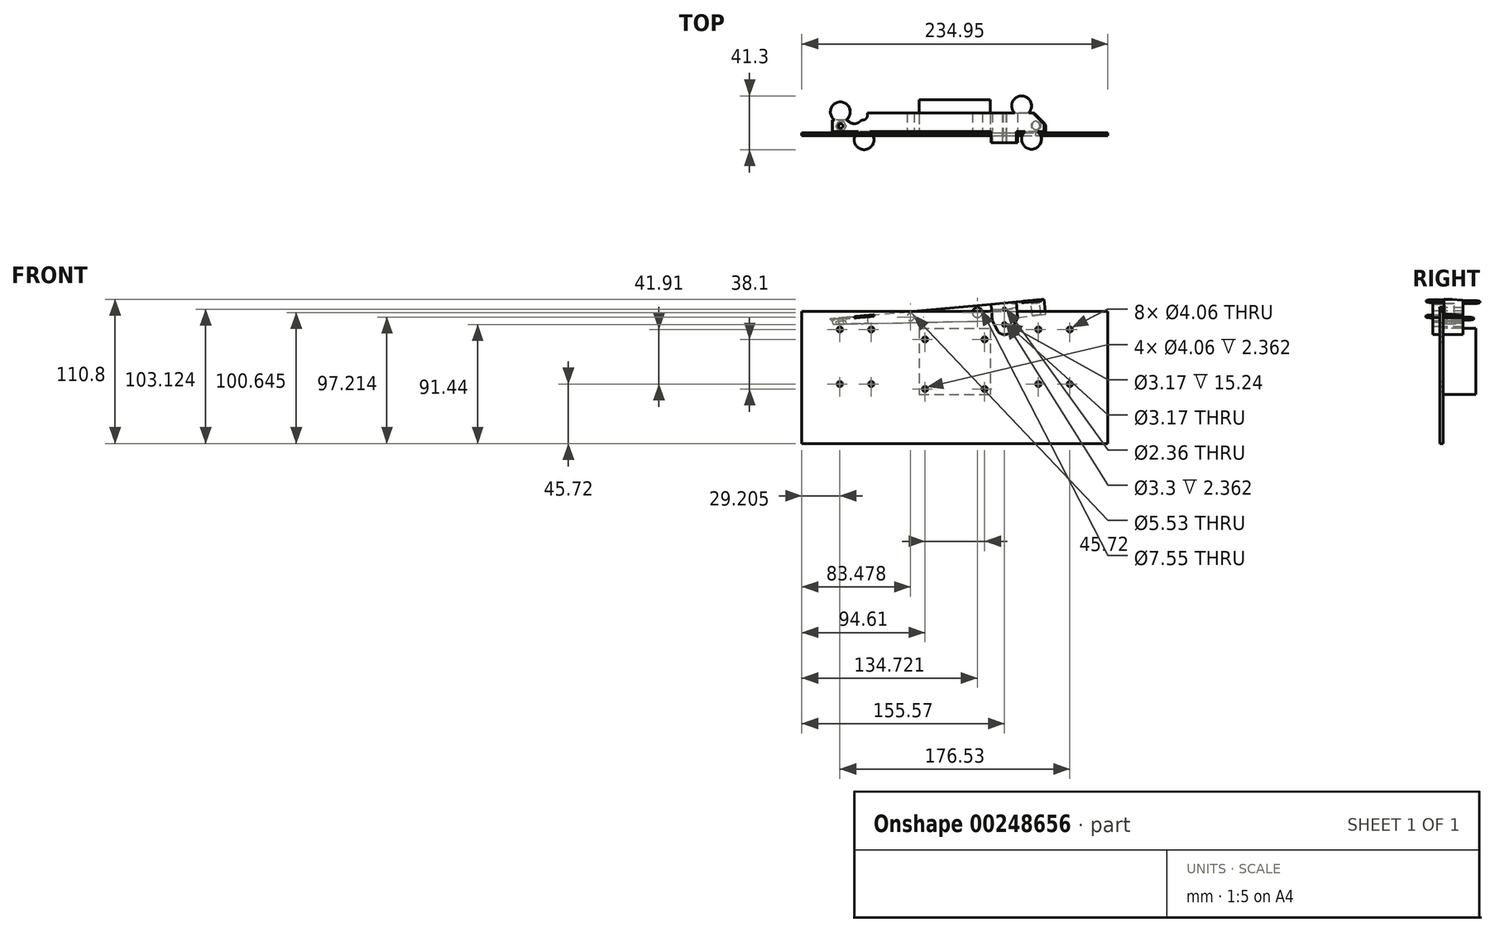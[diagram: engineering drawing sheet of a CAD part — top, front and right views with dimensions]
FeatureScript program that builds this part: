
annotation { "Feature Type Name" : "Feature", "Feature Type Description" : "" }
export const myFeature = defineFeature(function(context is Context, id is Id, definition is map)
    precondition{}
    {
        {
            var Q0;
            Q0=qCreatedBy(makeId("Front.planeOp"),FACE);
            var sketch = newSketch(context, id + "F0", { "sketchPlane" : qUnion([Q0])});
            skCircle(sketch, "E0", {"center": v(0, 0) * mm, "radius": 16.51 * mm, "construction": true});
            skLineSegment(sketch, "E1", {"start": v(-132.08, 4.54) * mm, "end": v(30.48, 19.36) * mm});
            skLineSegment(sketch, "E2", {"start": v(-132.08, 4.54) * mm, "end": v(-131.69, 0.24) * mm});
            skLineSegment(sketch, "E3", {"start": v(-131.69, 0.24) * mm, "end": v(-9.18, 2.82) * mm});
            skLineSegment(sketch, "E4", {"start": v(-9.18, 2.82) * mm, "end": v(-3.8, -7.62) * mm});
            skLineSegment(sketch, "E5", {"start": v(-3.8, -7.62) * mm, "end": v(3.81, -7.62) * mm});
            skLineSegment(sketch, "E6", {"start": v(3.8, -7.62) * mm, "end": v(10.05, 5.45) * mm});
            skLineSegment(sketch, "E7", {"start": v(10.05, 5.45) * mm, "end": v(31.52, 7.97) * mm});
            skLineSegment(sketch, "E8", {"start": v(31.52, 7.97) * mm, "end": v(30.48, 19.36) * mm});
            skCircle(sketch, "E9", {"center": v(0, 0) * mm, "radius": 1.59 * mm});
            skCircle(sketch, "E10", {"center": v(0, 0) * mm, "radius": 11.43 * mm, "construction": true});
            skLineSegment(sketch, "E11", {"start": v(-131.97, 3.37) * mm, "end": v(-0.3, 11.43) * mm});
            skLineSegment(sketch, "E12", {"start": v(-0.3, 11.43) * mm, "end": v(30.64, 17.62) * mm});
            skLineSegment(sketch, "E13", {"start": v(-9.18, 2.82) * mm, "end": v(-9.92, 10.84) * mm});
            skLineSegment(sketch, "E14", {"start": v(10.05, 5.45) * mm, "end": v(9.33, 13.35) * mm});
            skLineSegment(sketch, "E15", {"start": v(-9.92, 10.84) * mm, "end": v(-10.35, 15.63) * mm});
            skLineSegment(sketch, "E16", {"start": v(9.33, 13.35) * mm, "end": v(8.96, 17.4) * mm});
            skSolve(sketch);
        }
        {
            var Q0;
            {var subQ0=sQuery(id+"F0.wireOp",EDGE,"E3");Q0=makeQuery(id+"F0.imprint","IMPRINT",FACE,{"disambiguationData":[TD([[makeQuery(id+"F0.imprint","IMPRINT",EDGE,{"derivedFrom":subQ0}),1.0]])]});}
            var Q1;
            {var subQ3=sQuery(id+"F0.wireOp",EDGE,"E15");Q1=makeQuery(id+"F0.imprint","IMPRINT",FACE,{"disambiguationData":[TD([[makeQuery(id+"F0.imprint","IMPRINT",EDGE,{"derivedFrom":subQ3}),1.0]])]});}
            var Q2;
            {var subQ0=sQuery(id+"F0.wireOp",EDGE,"E15");Q2=makeQuery(id+"F0.imprint","IMPRINT",FACE,{"disambiguationData":[TD([[makeQuery(id+"F0.imprint","IMPRINT",EDGE,{"derivedFrom":subQ0}),-1.0]])]});}
            var Q3;
            Q3=makeQuery(id+"F0.imprint","IMPRINT",FACE,{"disambiguationData":[TD([[makeQuery(id+"F0.imprint","IMPRINT",EDGE,{"derivedFrom":sQuery(id+"F0.wireOp",EDGE,"E4")}),1.0]])]});
            var Q4;
            {var subQ0=sQuery(id+"F0.wireOp",EDGE,"E7");Q4=makeQuery(id+"F0.imprint","IMPRINT",FACE,{"disambiguationData":[TD([[makeQuery(id+"F0.imprint","IMPRINT",EDGE,{"derivedFrom":subQ0}),1.0]])]});}
            var Q5;
            {var subQ3=sQuery(id+"F0.wireOp",EDGE,"E16");Q5=makeQuery(id+"F0.imprint","IMPRINT",FACE,{"disambiguationData":[TD([[makeQuery(id+"F0.imprint","IMPRINT",EDGE,{"derivedFrom":subQ3}),-1.0]])]});}
            extrude(context, id + "F1", {"entities" : qUnion([Q0, Q1, Q2, Q3, Q4, Q5]), "oppositeDirection" : true, "depth" : 15.24 * mm, "hasSecondDirection" : true, "secondDirectionOppositeDirection" : false, "secondDirectionDepth" : 7.62 * mm});
        }
        {
            var Q0;
            {var subQ1=sQuery(id+"F0.wireOp",EDGE,"E3");Q0=makeQuery(id+"F0.imprint","IMPRINT",FACE,{"disambiguationData":[TD([[makeQuery(id+"F0.imprint","IMPRINT",EDGE,{"derivedFrom":subQ1}),1.0]])]});}
            var Q1;
            Q1=makeQuery(id+"F0.imprint","IMPRINT",FACE,{"disambiguationData":[TD([[makeQuery(id+"F0.imprint","IMPRINT",EDGE,{"derivedFrom":sQuery(id+"F0.wireOp",EDGE,"E4")}),1.0]])]});
            var Q2;
            {var subQ0=sQuery(id+"F0.wireOp",EDGE,"E7");Q2=makeQuery(id+"F0.imprint","IMPRINT",FACE,{"disambiguationData":[TD([[makeQuery(id+"F0.imprint","IMPRINT",EDGE,{"derivedFrom":subQ0}),1.0]])]});}
            extrude(context, id + "F2", {"entities" : qUnion([Q0, Q1, Q2]), "operationType" : NewBodyOperationType.REMOVE, "depth" : 2.5 * mm});
        }
        {
            var Q0;
            {var subQ0=sQuery(id+"F0.wireOp",EDGE,"E3");Q0=makeQuery(id+"F0.imprint","IMPRINT",FACE,{"disambiguationData":[TD([[makeQuery(id+"F0.imprint","IMPRINT",EDGE,{"derivedFrom":subQ0}),1.0]])]});}
            var Q1;
            {var subQ3=sQuery(id+"F0.wireOp",EDGE,"E15");Q1=makeQuery(id+"F0.imprint","IMPRINT",FACE,{"disambiguationData":[TD([[makeQuery(id+"F0.imprint","IMPRINT",EDGE,{"derivedFrom":subQ3}),1.0]])]});}
            var Q2;
            {var subQ0=sQuery(id+"F0.wireOp",EDGE,"E7");Q2=makeQuery(id+"F0.imprint","IMPRINT",FACE,{"disambiguationData":[TD([[makeQuery(id+"F0.imprint","IMPRINT",EDGE,{"derivedFrom":subQ0}),1.0]])]});}
            var Q3;
            {var subQ3=sQuery(id+"F0.wireOp",EDGE,"E16");Q3=makeQuery(id+"F0.imprint","IMPRINT",FACE,{"disambiguationData":[TD([[makeQuery(id+"F0.imprint","IMPRINT",EDGE,{"derivedFrom":subQ3}),-1.0]])]});}
            extrude(context, id + "F3", {"entities" : qUnion([Q0, Q1, Q2, Q3]), "operationType" : NewBodyOperationType.REMOVE, "depth" : 25.4 * mm, "hasSecondDirection" : true, "secondDirectionOppositeDirection" : true, "secondDirectionDepth" : 0.76 * mm});
        }
        {
            var Q0;
            {var subQ0=sQuery(id+"F0.wireOp",EDGE,"E9");var subQ1=sQuery(id+"F0.wireOp",EDGE,"E8");var subQ2=sQuery(id+"F0.wireOp",EDGE,"E7");var subQ3=sQuery(id+"F0.wireOp",EDGE,"E6");var subQ4=sQuery(id+"F0.wireOp",EDGE,"E5");var subQ5=sQuery(id+"F0.wireOp",EDGE,"E4");var subQ6=sQuery(id+"F0.wireOp",EDGE,"E3");var subQ7=sQuery(id+"F0.wireOp",EDGE,"E2");Q0=makeQuery(id+"F2.boolean.opBoolean","SPLIT",EDGE,{"disambiguationData":[TD([makeQuery(id+"F1.opExtrude","CAP_FACE",FACE,{"disambiguationData":[OSD([sQuery(id+"F0.wireOp",EDGE,"E1"),subQ7,subQ6,subQ5,subQ4,subQ3,subQ2,subQ1,subQ0])],"isStart":false})])],"derivedFrom":makeQuery(id+"F1.opExtrude","SWEPT_EDGE",EDGE,{"disambiguationData":[OSD([subQ5,subQ4])]})});}
            var Q1;
            {var subQ0=sQuery(id+"F0.wireOp",EDGE,"E9");var subQ1=sQuery(id+"F0.wireOp",EDGE,"E8");var subQ2=sQuery(id+"F0.wireOp",EDGE,"E7");var subQ3=sQuery(id+"F0.wireOp",EDGE,"E6");var subQ4=sQuery(id+"F0.wireOp",EDGE,"E5");var subQ5=sQuery(id+"F0.wireOp",EDGE,"E4");var subQ6=sQuery(id+"F0.wireOp",EDGE,"E3");var subQ7=sQuery(id+"F0.wireOp",EDGE,"E2");Q1=makeQuery(id+"F2.boolean.opBoolean","SPLIT",EDGE,{"disambiguationData":[TD([makeQuery(id+"F1.opExtrude","CAP_FACE",FACE,{"disambiguationData":[OSD([sQuery(id+"F0.wireOp",EDGE,"E1"),subQ7,subQ6,subQ5,subQ4,subQ3,subQ2,subQ1,subQ0])],"isStart":true})])],"derivedFrom":makeQuery(id+"F1.opExtrude","SWEPT_EDGE",EDGE,{"disambiguationData":[OSD([subQ5,subQ4])]})});}
            var Q2;
            {var subQ0=sQuery(id+"F0.wireOp",EDGE,"E9");var subQ1=sQuery(id+"F0.wireOp",EDGE,"E8");var subQ2=sQuery(id+"F0.wireOp",EDGE,"E7");var subQ3=sQuery(id+"F0.wireOp",EDGE,"E6");var subQ4=sQuery(id+"F0.wireOp",EDGE,"E5");var subQ5=sQuery(id+"F0.wireOp",EDGE,"E4");var subQ6=sQuery(id+"F0.wireOp",EDGE,"E3");var subQ7=sQuery(id+"F0.wireOp",EDGE,"E2");Q2=makeQuery(id+"F2.boolean.opBoolean","SPLIT",EDGE,{"disambiguationData":[TD([makeQuery(id+"F1.opExtrude","CAP_FACE",FACE,{"disambiguationData":[OSD([sQuery(id+"F0.wireOp",EDGE,"E1"),subQ7,subQ6,subQ5,subQ4,subQ3,subQ2,subQ1,subQ0])],"isStart":true})])],"derivedFrom":makeQuery(id+"F1.opExtrude","SWEPT_EDGE",EDGE,{"disambiguationData":[OSD([subQ4,subQ3])]})});}
            var Q3;
            {var subQ0=sQuery(id+"F0.wireOp",EDGE,"E9");var subQ1=sQuery(id+"F0.wireOp",EDGE,"E8");var subQ2=sQuery(id+"F0.wireOp",EDGE,"E7");var subQ3=sQuery(id+"F0.wireOp",EDGE,"E6");var subQ4=sQuery(id+"F0.wireOp",EDGE,"E5");var subQ5=sQuery(id+"F0.wireOp",EDGE,"E4");var subQ6=sQuery(id+"F0.wireOp",EDGE,"E3");var subQ7=sQuery(id+"F0.wireOp",EDGE,"E2");Q3=makeQuery(id+"F2.boolean.opBoolean","SPLIT",EDGE,{"disambiguationData":[TD([makeQuery(id+"F1.opExtrude","CAP_FACE",FACE,{"disambiguationData":[OSD([sQuery(id+"F0.wireOp",EDGE,"E1"),subQ7,subQ6,subQ5,subQ4,subQ3,subQ2,subQ1,subQ0])],"isStart":false})])],"derivedFrom":makeQuery(id+"F1.opExtrude","SWEPT_EDGE",EDGE,{"disambiguationData":[OSD([subQ4,subQ3])]})});}
            fillet(context, id + "F4", {"entities" : qUnion([Q0, Q1, Q2, Q3]), "radius" : 5.08 * mm, "tangentPropagation" : true, "allowEdgeOverflow" : false});
        }
        {
            var Q0;
            Q0=makeQuery(id+"F1.opExtrude","SWEPT_FACE",FACE,{"disambiguationData":[OSD([sQuery(id+"F0.wireOp",EDGE,"E1")])]});
            var sketch = newSketch(context, id + "F5", { "sketchPlane" : qUnion([Q0])});
            skCircle(sketch, "E17", {"center": v(-124.77, 5.08) * mm, "radius": 1.77 * mm});
            skSolve(sketch);
        }
        {
            var Q0;
            Q0 = qSketchRegion(id + "F5", true);
            extrude(context, id + "F6", {"entities" : qUnion([Q0]), "operationType" : NewBodyOperationType.REMOVE, "endBound" : BoundingType.THROUGH_ALL, "oppositeDirection" : true, "depth" : 25.4 * mm});
        }
        {
            var Q0;
            Q0=qCreatedBy(makeId("Front.planeOp"),FACE);
            var sketch = newSketch(context, id + "F7", { "sketchPlane" : qUnion([Q0])});
            skLineSegment(sketch, "E18.bottom", {"start": v(-155.58, 10.16) * mm, "end": v(79.38, 10.16) * mm});
            skLineSegment(sketch, "E18.top", {"start": v(-155.58, -91.44) * mm, "end": v(79.38, -91.44) * mm});
            skLineSegment(sketch, "E18.left", {"start": v(-155.58, 10.16) * mm, "end": v(-155.58, -91.44) * mm});
            skLineSegment(sketch, "E18.right", {"start": v(79.38, 10.16) * mm, "end": v(79.38, -91.44) * mm});
            skPoint(sketch, "E19", {"position": v(-38.1, 10.16) * mm});
            skLineSegment(sketch, "E20.bottom", {"start": v(-60.96, -11.43) * mm, "end": v(-15.24, -11.43) * mm, "construction": true});
            skLineSegment(sketch, "E20.top", {"start": v(-60.96, -49.53) * mm, "end": v(-15.24, -49.53) * mm, "construction": true});
            skLineSegment(sketch, "E20.left", {"start": v(-60.96, -11.43) * mm, "end": v(-60.96, -49.53) * mm, "construction": true});
            skLineSegment(sketch, "E20.right", {"start": v(-15.24, -11.43) * mm, "end": v(-15.24, -49.53) * mm, "construction": true});
            skPoint(sketch, "E20.middle", {"position": v(-38.1, -30.48) * mm});
            skCircle(sketch, "E21", {"center": v(-60.96, -11.43) * mm, "radius": 2.03 * mm});
            skCircle(sketch, "E22", {"center": v(-15.24, -11.43) * mm, "radius": 2.03 * mm});
            skCircle(sketch, "E23", {"center": v(-60.96, -49.53) * mm, "radius": 2.03 * mm});
            skCircle(sketch, "E24", {"center": v(-15.24, -49.53) * mm, "radius": 2.03 * mm});
            skLineSegment(sketch, "E25", {"start": v(-114.3, -3.81) * mm, "end": v(-114.3, -45.72) * mm, "construction": true});
            skLineSegment(sketch, "E26", {"start": v(38.1, -3.81) * mm, "end": v(38.1, -45.72) * mm, "construction": true});
            skLineSegment(sketch, "E27", {"start": v(-114.3, -3.81) * mm, "end": v(38.1, -3.81) * mm, "construction": true});
            skLineSegment(sketch, "E28", {"start": v(-114.3, -45.72) * mm, "end": v(38.1, -45.72) * mm, "construction": true});
            skCircle(sketch, "E29", {"center": v(0, 0) * mm, "radius": 1.65 * mm});
            skLineSegment(sketch, "E30.bottom", {"start": v(-102.23, -3.81) * mm, "end": v(-126.37, -3.81) * mm, "construction": true});
            skLineSegment(sketch, "E30.top", {"start": v(-102.23, -45.72) * mm, "end": v(-126.37, -45.72) * mm, "construction": true});
            skLineSegment(sketch, "E30.left", {"start": v(-102.23, -3.81) * mm, "end": v(-102.23, -45.72) * mm, "construction": true});
            skLineSegment(sketch, "E30.right", {"start": v(-126.37, -3.81) * mm, "end": v(-126.37, -45.72) * mm, "construction": true});
            skPoint(sketch, "E30.middle", {"position": v(-114.3, -24.77) * mm});
            skLineSegment(sketch, "E31.bottom", {"start": v(50.17, -3.81) * mm, "end": v(26.04, -3.81) * mm, "construction": true});
            skLineSegment(sketch, "E31.top", {"start": v(50.17, -45.72) * mm, "end": v(26.04, -45.72) * mm, "construction": true});
            skLineSegment(sketch, "E31.left", {"start": v(50.17, -3.81) * mm, "end": v(50.17, -45.72) * mm, "construction": true});
            skLineSegment(sketch, "E31.right", {"start": v(26.04, -3.81) * mm, "end": v(26.04, -45.72) * mm, "construction": true});
            skPoint(sketch, "E31.middle", {"position": v(38.1, -24.77) * mm});
            skCircle(sketch, "E32", {"center": v(-102.23, -3.81) * mm, "radius": 2.03 * mm});
            skCircle(sketch, "E33", {"center": v(-126.37, -3.81) * mm, "radius": 2.03 * mm});
            skCircle(sketch, "E34", {"center": v(-126.37, -45.72) * mm, "radius": 2.03 * mm});
            skCircle(sketch, "E35", {"center": v(-102.23, -45.72) * mm, "radius": 2.03 * mm});
            skCircle(sketch, "E36", {"center": v(26.04, -45.72) * mm, "radius": 2.03 * mm});
            skCircle(sketch, "E37", {"center": v(50.17, -45.72) * mm, "radius": 2.03 * mm});
            skCircle(sketch, "E38", {"center": v(50.17, -3.81) * mm, "radius": 2.03 * mm});
            skCircle(sketch, "E39", {"center": v(26.04, -3.81) * mm, "radius": 2.03 * mm});
            skSolve(sketch);
        }
        {
            var Q0;
            Q0 = qSketchRegion(id + "F7", true);
            extrude(context, id + "F8", {"entities" : qUnion([Q0]), "depth" : 2.36 * mm});
        }
        {
            var Q0;
            Q0=makeQuery(id+"F1.opExtrude","SWEPT_FACE",FACE,{"disambiguationData":[OSD([sQuery(id+"F0.wireOp",EDGE,"E1")])]});
            var sketch = newSketch(context, id + "F9", { "sketchPlane" : qUnion([Q0])});
            skLineSegment(sketch, "E40.bottom", {"start": v(-131.12, 15.24) * mm, "end": v(-104.22, 15.24) * mm});
            skLineSegment(sketch, "E40.top", {"start": v(-131.12, 9.65) * mm, "end": v(-107.77, 9.65) * mm});
            skLineSegment(sketch, "E40.left", {"start": v(-131.12, 15.24) * mm, "end": v(-131.12, 9.65) * mm});
            skLineSegment(sketch, "E40.right", {"start": v(-104.22, 15.24) * mm, "end": v(-104.22, 13.2) * mm});
            skPoint(sketch, "E41.visualSharp", {"position": v(-104.22, 9.65) * mm});
            skArc(sketch, "E41.filletArc", {"start": v(-107.77, 9.65) * mm, "mid": v(-105.26, 10.7) * mm, "end": v(-104.22, 13.2) * mm});
            skCircle(sketch, "E42", {"center": v(-114.36, 13.46) * mm, "radius": 6.6 * mm});
            skSolve(sketch);
        }
        {
            var Q0;
            Q0 = qSketchRegion(id + "F9", true);
            extrude(context, id + "F10", {"entities" : qUnion([Q0]), "operationType" : NewBodyOperationType.REMOVE, "endBound" : BoundingType.THROUGH_ALL, "oppositeDirection" : true, "depth" : 25.4 * mm});
        }
        {
            var Q0;
            Q0=makeQuery(id+"F7.imprint","IMPRINT",FACE,{"disambiguationData":[TD([[makeQuery(id+"F7.imprint","IMPRINT",EDGE,{"derivedFrom":sQuery(id+"F7.wireOp",EDGE,"E18.bottom")}),-1.0]])]});
            var sketch = newSketch(context, id + "F11", { "sketchPlane" : qUnion([Q0])});
            skLineSegment(sketch, "E43.bottom", {"start": v(-65.4, -3.05) * mm, "end": v(-10.8, -3.05) * mm});
            skLineSegment(sketch, "E43.top", {"start": v(-65.4, -53.85) * mm, "end": v(-10.8, -53.85) * mm});
            skLineSegment(sketch, "E43.left", {"start": v(-65.4, -3.05) * mm, "end": v(-65.4, -53.85) * mm});
            skLineSegment(sketch, "E43.right", {"start": v(-10.8, -3.05) * mm, "end": v(-10.8, -53.85) * mm});
            skPoint(sketch, "E43.middle", {"position": v(-38.1, -28.45) * mm});
            skLineSegment(sketch, "E44.0", {"start": v(-155.58, 10.16) * mm, "end": v(79.38, 10.16) * mm, "construction": true});
            skLineSegment(sketch, "E45", {"start": v(-38.1, 10.16) * mm, "end": v(-38.1, -57.27) * mm, "construction": true});
            skPoint(sketch, "E46", {"position": v(-38.1, -53.85) * mm});
            skPoint(sketch, "E47", {"position": v(-38.1, -18.36) * mm});
            skSolve(sketch);
        }
        {
            var Q0;
            Q0 = qSketchRegion(id + "F11", true);
            extrude(context, id + "F12", {"entities" : qUnion([Q0]), "operationType" : NewBodyOperationType.ADD, "oppositeDirection" : true, "depth" : 25.4 * mm});
        }
        {
            var Q0;
            Q0=makeQuery(id+"F1.opExtrude","SWEPT_FACE",FACE,{"disambiguationData":[OSD([sQuery(id+"F0.wireOp",EDGE,"E1")])]});
            cPlane(context, id + "F13", {"entities" : qUnion([Q0]), "cplaneType" : CPlaneType.OFFSET, "offset" : 2.54 * mm, "oppositeDirection" : true, "width" : 152.4 * mm, "height" : 152.4 * mm});
        }
        {
            var Q0;
            Q0=qCreatedBy(id+"F13.planeOp",FACE);
            var sketch = newSketch(context, id + "F14", { "sketchPlane" : qUnion([Q0])});
            skCircle(sketch, "E48.0", {"center": v(-124.77, 5.08) * mm, "radius": 1.77 * mm});
            skCircle(sketch, "E49.cCircle", {"center": v(-124.77, 5.08) * mm, "radius": 3.3 * mm, "construction": true});
            skLineSegment(sketch, "E49.0", {"start": v(-126.68, 1.78) * mm, "end": v(-128.59, 5.08) * mm});
            skLineSegment(sketch, "E49.1", {"start": v(-128.59, 5.08) * mm, "end": v(-126.68, 8.38) * mm});
            skLineSegment(sketch, "E49.2", {"start": v(-126.68, 8.38) * mm, "end": v(-122.87, 8.38) * mm});
            skLineSegment(sketch, "E49.3", {"start": v(-122.87, 8.38) * mm, "end": v(-120.96, 5.08) * mm});
            skLineSegment(sketch, "E49.4", {"start": v(-120.96, 5.08) * mm, "end": v(-122.87, 1.78) * mm});
            skLineSegment(sketch, "E49.5", {"start": v(-122.87, 1.78) * mm, "end": v(-126.68, 1.78) * mm});
            skPoint(sketch, "E49.0.midPoint", {"position": v(-128.07, 5.08) * mm});
            skSolve(sketch);
        }
        {
            var Q0;
            Q0 = qSketchRegion(id + "F14", true);
            extrude(context, id + "F15", {"entities" : qUnion([Q0]), "operationType" : NewBodyOperationType.REMOVE, "oppositeDirection" : true, "depth" : 25.4 * mm});
        }
        {
            var Q0;
            Q0=qCreatedBy(id+"F13.planeOp",FACE);
            var sketch = newSketch(context, id + "F16", { "sketchPlane" : qUnion([Q0])});
            skCircle(sketch, "E50", {"center": v(25.15, 5.33) * mm, "radius": 3.3 * mm});
            skSolve(sketch);
        }
        {
            var Q0;
            Q0 = qSketchRegion(id + "F16", true);
            extrude(context, id + "F17", {"entities" : qUnion([Q0]), "operationType" : NewBodyOperationType.REMOVE, "oppositeDirection" : true, "depth" : 25.4 * mm});
        }
        {
            var Q0;
            Q0=makeQuery(id+"F1.opExtrude","CAP_EDGE",EDGE,{"disambiguationData":[OSD([sQuery(id+"F0.wireOp",EDGE,"E8")])],"isStart":false});
            chamfer(context, id + "F18", {"entities" : qUnion([Q0]), "width" : 8.9 * mm, "tangentPropagation" : true});
        }
        {
            var Q0;
            Q0=makeQuery(id+"F1.opExtrude","CAP_FACE",FACE,{"disambiguationData":[OSD([sQuery(id+"F0.wireOp",EDGE,"E1"),sQuery(id+"F0.wireOp",EDGE,"E2"),sQuery(id+"F0.wireOp",EDGE,"E3"),sQuery(id+"F0.wireOp",EDGE,"E4"),sQuery(id+"F0.wireOp",EDGE,"E5"),sQuery(id+"F0.wireOp",EDGE,"E6"),sQuery(id+"F0.wireOp",EDGE,"E7"),sQuery(id+"F0.wireOp",EDGE,"E8"),sQuery(id+"F0.wireOp",EDGE,"E9")])],"isStart":true});
            var sketch = newSketch(context, id + "F19", { "sketchPlane" : qUnion([Q0])});
            skCircle(sketch, "E51", {"center": v(0, 11.68) * mm, "radius": 1.18 * mm});
            skSolve(sketch);
        }
        {
            var Q0;
            Q0 = qSketchRegion(id + "F19", true);
            extrude(context, id + "F20", {"entities" : qUnion([Q0]), "operationType" : NewBodyOperationType.REMOVE, "oppositeDirection" : true, "depth" : 48.26 * mm});
        }
        {
            var Q0;
            Q0=makeQuery(id+"F2.boolean.opBoolean","COPY",EDGE,{"derivedFrom":makeQuery(id+"F2.opExtrude","CAP_EDGE",EDGE,{"disambiguationData":[OSD([sQuery(id+"F0.wireOp",EDGE,"E12")])],"isStart":true})});
            var Q1;
            Q1=makeQuery(id+"F2.boolean.opBoolean","COPY",EDGE,{"derivedFrom":makeQuery(id+"F2.opExtrude","CAP_EDGE",EDGE,{"disambiguationData":[OSD([sQuery(id+"F0.wireOp",EDGE,"E12")])],"isStart":false})});
            fillet(context, id + "F21", {"entities" : qUnion([Q0, Q1]), "radius" : 0.76 * mm, "tangentPropagation" : true, "allowEdgeOverflow" : false});
        }
        {
            var Q0;
            Q0=makeQuery(id+"F3.boolean.opBoolean","COPY",EDGE,{"derivedFrom":makeQuery(id+"F3.opExtrude","CAP_EDGE",EDGE,{"disambiguationData":[OSD([sQuery(id+"F0.wireOp",EDGE,"E8")])],"isStart":true})});
            var Q1;
            {var subQ0=sQuery(id+"F0.wireOp",EDGE,"E8");Q1=makeQuery(id+"F18.opChamfer","BLEND_EDGE",EDGE,{"blendedFrom":[makeQuery(id+"F1.opExtrude","CAP_EDGE",EDGE,{"disambiguationData":[OSD([subQ0])],"isStart":false}),makeQuery(id+"F1.opExtrude","SWEPT_FACE",FACE,{"disambiguationData":[OSD([subQ0])]})],"blendedInto":[makeQuery(id+"F1.opExtrude","SWEPT_FACE",FACE,{"disambiguationData":[OSD([subQ0])]})]});}
            var Q2;
            {var subQ0=sQuery(id+"F0.wireOp",EDGE,"E8");Q2=makeQuery(id+"F18.opChamfer","BLEND_EDGE",EDGE,{"blendedFrom":[makeQuery(id+"F1.opExtrude","CAP_EDGE",EDGE,{"disambiguationData":[OSD([subQ0])],"isStart":false}),makeQuery(id+"F1.opExtrude","CAP_FACE",FACE,{"disambiguationData":[OSD([sQuery(id+"F0.wireOp",EDGE,"E1"),sQuery(id+"F0.wireOp",EDGE,"E2"),sQuery(id+"F0.wireOp",EDGE,"E3"),sQuery(id+"F0.wireOp",EDGE,"E4"),sQuery(id+"F0.wireOp",EDGE,"E5"),sQuery(id+"F0.wireOp",EDGE,"E6"),sQuery(id+"F0.wireOp",EDGE,"E7"),subQ0,sQuery(id+"F0.wireOp",EDGE,"E9")])],"isStart":false})],"blendedInto":[makeQuery(id+"F1.opExtrude","CAP_FACE",FACE,{"disambiguationData":[OSD([sQuery(id+"F0.wireOp",EDGE,"E1"),sQuery(id+"F0.wireOp",EDGE,"E2"),sQuery(id+"F0.wireOp",EDGE,"E3"),sQuery(id+"F0.wireOp",EDGE,"E4"),sQuery(id+"F0.wireOp",EDGE,"E5"),sQuery(id+"F0.wireOp",EDGE,"E6"),sQuery(id+"F0.wireOp",EDGE,"E7"),subQ0,sQuery(id+"F0.wireOp",EDGE,"E9")])],"isStart":false})]});}
            var Q3;
            Q3=makeQuery(id+"F10.boolean.opBoolean","COPY",EDGE,{"derivedFrom":makeQuery(id+"F10.opExtrude","SWEPT_EDGE",EDGE,{"disambiguationData":[OSD([sQuery(id+"F0.wireOp",EDGE,"E1"),sQuery(id+"F0.wireOp",EDGE,"E2"),sQuery(id+"F9.wireOp",EDGE,"E40.top"),sQuery(id+"F9.wireOp",EDGE,"E40.left")])]})});
            var Q4;
            {var subQ0=sQuery(id+"F9.wireOp",EDGE,"E42");var subQ1=sQuery(id+"F9.wireOp",EDGE,"E40.top");Q4=makeQuery(id+"F10.boolean.opBoolean","COPY",EDGE,{"derivedFrom":makeQuery(id+"F10.opExtrude","SWEPT_EDGE",EDGE,{"disambiguationData":[OSD([subQ1,subQ0]),TDD([makeQuery(id+"F9.imprint","INTERSECT",VERTEX,{"disambiguationData":[OD(0.0)],"derivedFrom":[subQ1,subQ0]})])]})});}
            var Q5;
            {var subQ0=sQuery(id+"F9.wireOp",EDGE,"E42");var subQ1=sQuery(id+"F9.wireOp",EDGE,"E40.top");Q5=makeQuery(id+"F10.boolean.opBoolean","COPY",EDGE,{"derivedFrom":makeQuery(id+"F10.opExtrude","SWEPT_EDGE",EDGE,{"disambiguationData":[OSD([subQ1,subQ0]),TDD([makeQuery(id+"F9.imprint","INTERSECT",VERTEX,{"disambiguationData":[OD(1.0)],"derivedFrom":[subQ1,subQ0]})])]})});}
            var Q6;
            Q6=makeQuery(id+"F10.boolean.opBoolean","COPY",EDGE,{"derivedFrom":makeQuery(id+"F10.opExtrude","SWEPT_EDGE",EDGE,{"disambiguationData":[OSD([sQuery(id+"F0.wireOp",EDGE,"E1"),sQuery(id+"F9.wireOp",EDGE,"E40.bottom"),sQuery(id+"F9.wireOp",EDGE,"E40.right")])]})});
            var Q7;
            Q7=makeQuery(id+"F3.boolean.opBoolean","COPY",EDGE,{"derivedFrom":makeQuery(id+"F3.opExtrude","CAP_EDGE",EDGE,{"disambiguationData":[OSD([sQuery(id+"F0.wireOp",EDGE,"E2")])],"isStart":true})});
            fillet(context, id + "F22", {"entities" : qUnion([Q0, Q1, Q2, Q3, Q4, Q5, Q6, Q7]), "radius" : 2.54 * mm, "tangentPropagation" : true, "allowEdgeOverflow" : false});
        }
        {
            var Q0;
            Q0=makeQuery(id+"F1.opExtrude","SWEPT_FACE",FACE,{"disambiguationData":[OSD([sQuery(id+"F0.wireOp",EDGE,"E1")])]});
            var sketch = newSketch(context, id + "F23", { "sketchPlane" : qUnion([Q0])});
            skCircle(sketch, "E52", {"center": v(14.68, 20.64) * mm, "radius": 7.62 * mm});
            skCircle(sketch, "E53", {"center": v(22.31, -5.1) * mm, "radius": 7.62 * mm});
            skCircle(sketch, "E54", {"center": v(-106.76, -5.42) * mm, "radius": 7.62 * mm});
            skCircle(sketch, "E55", {"center": v(-125.1, 15.99) * mm, "radius": 7.62 * mm});
            skSolve(sketch);
        }
        {
            var Q0;
            Q0 = qSketchRegion(id + "F23", true);
            extrude(context, id + "F24", {"entities" : qUnion([Q0]), "operationType" : NewBodyOperationType.ADD, "oppositeDirection" : true, "depth" : 1.02 * mm});
        }
        {
            var Q0;
            Q0=qCreatedBy(makeId("Front.planeOp"),FACE);
            var sketch = newSketch(context, id + "F25", { "sketchPlane" : qUnion([Q0])});
            skCircle(sketch, "E56", {"center": v(-20.85, 9.2) * mm, "radius": 3.77 * mm});
            skCircle(sketch, "E57", {"center": v(-72.1, 5.77) * mm, "radius": 2.76 * mm});
            skSolve(sketch);
        }
        {
            var Q0;
            Q0 = qSketchRegion(id + "F25", true);
            extrude(context, id + "F26", {"entities" : qUnion([Q0]), "operationType" : NewBodyOperationType.REMOVE, "endBound" : BoundingType.THROUGH_ALL, "oppositeDirection" : true, "depth" : 25.4 * mm});
        }
    });
